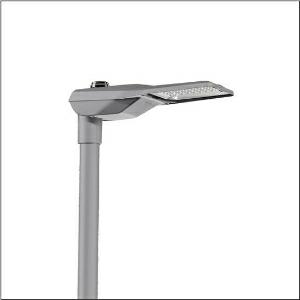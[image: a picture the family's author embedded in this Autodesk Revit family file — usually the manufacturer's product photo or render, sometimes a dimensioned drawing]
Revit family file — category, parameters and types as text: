
# Revit family: streetlight_sl_21_mini___st0_5a_5xe6b37n08jb_3e92
name_source: partatom
category: Lighting Fixtures
units: mm (PartAtom-declared; Revit-internal decimal feet)

## family parameters
Cut with Voids When Loaded = No
Host = Face
Light Source = No
Part Type = Normal
Room Calculation Point = No
Round Connector Dimension = Use Diameter
Shared = No

## types (1)
- --- (1 x LED, 12830 lm, 87.3 W, 3000K)
    Apparent Load = 87 VA
    CIE Flux Codes = 43 76 97 100 100
    Color Rendering = 70
    Color Temperature = 3000K
    Default Elevation = 1800 mm
    Description = Streetlight SL 21 mini, mast luminaire, primary light control with lens, of PMMA, primary optical cover: cover, of toughened safety glass, transparent, light distribution: ST0.5a, light emission: direct distribution, primary light characteristic: asymmetric, installation type: side-entry, LED, 3G 2.5mm², High Power LED, rated luminous flux: 12.830lm, luminous efficacy: 147lm/W, light colour: 730, colour temperature: 3000K, control gear: NEMA (7pin), control: overheat protection, pre-setting: linear dimming characteristic, constant luminous flux control, time-dependent luminous flux control, flexible luminous flux parameterisation, mains connection: 230..240V, AC, 50/60Hz, connection cable pre-assembled, cable length: 10,5m, wiring characteristics: H05VV-F, start of lifetime: 87W, end of service life: 90W, reduction: 40W, luminaire housing, of diecast aluminium (EN AC-44300), powder-coated, Siteco® metallic grey (DB 702S), corrosivity category C5 mid according to DIN EN ISO 12944, multi-level sealing system, sealing non-destructively replaceable, inclination adjustable: 0°, 5°, 10°, 15°, length: 628mm, width: 235mm, height: 110mm, spigot size: 42mm (side-entry), mounting height: 4..8m, protection rating (complete): IP66, insulation class (complete): insulation class I (protective earthing), certification: CE, ENEC, ENEC+, VDE, impact resistance: IK10, permissible operating ambient temperature for outdoor applications: -40..+50°C, standard-compliant lighting for roads and squares, packaging unit: 1 piece

Light Distribution: ST0.5a
    Height = 110 mm
    Lamp = 1 x LED
    Lamp Light Flux = 12830 lm
    Lamp Power = 87.3 W
    Lamp count = 1
    Length = 625 mm
    Luminous efficacy = 147 lm/W
    Manufacturer = Siteco
    ModVariant = No
    Model = 5XE6B37N08JB
    Number of Poles = 1
    OnlyDefault = Yes
    Power Factor = 1
    Product Name = Streetlight SL 21 mini | ST0.5a
    Product group = mast luminaire | pylon top
    ProductGroupID = 6100
    Protection Class = Protection class I
    Protection Degree = IP 66
    RLX_Detail_Level = 1
    RLX_Emergency_Light_Flux = 0 lm
    RLX_Emergency_Type = 0
    RLX_Emergency_Type_DB = No
    RlxData = <blob elided: 37177 chars, md5=174e7341>
    Socket = socket
    Standby Power = 0 W
    System Light Flux = 12830 lm
    System Power = 87 W
    Type Comments = factory setting: luminous flux: 100 % | dim-lin: 254 | 915 mA
    Type Image = l_1294379.jpg
    URL = http://relux.com
    VarID = @adj_158249
    Voltage = 0 V
    Weight = 0.00 kg
    Width = 234 mm

## geometry (parser evidence)
native form markers: Blend x4, Sweep x10
no freeform markers — native parametric forms only
